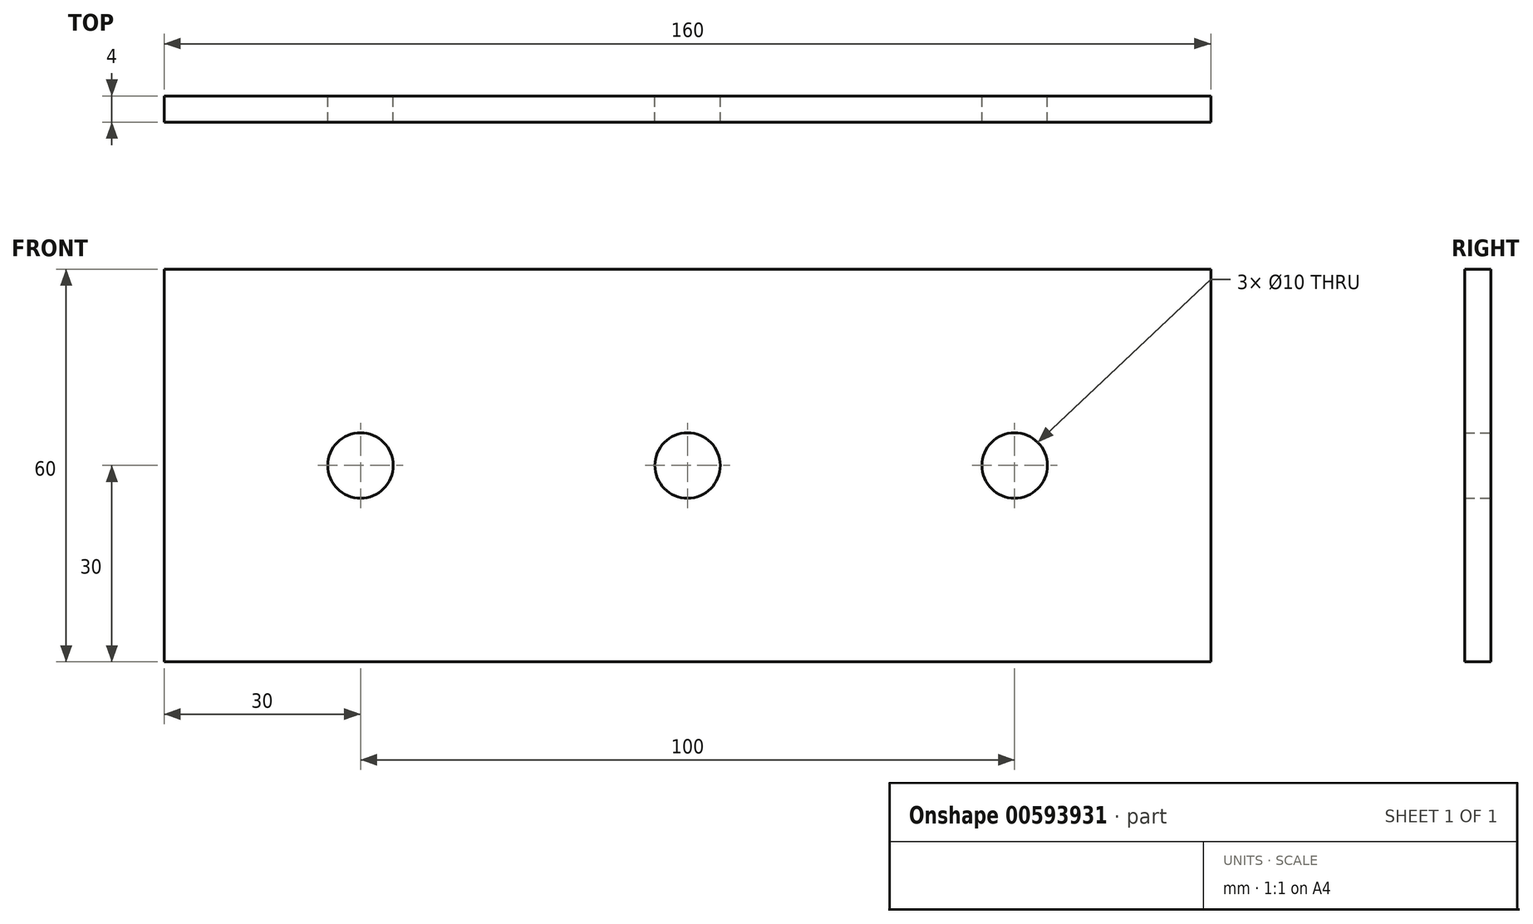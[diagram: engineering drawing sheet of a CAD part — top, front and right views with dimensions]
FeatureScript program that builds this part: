
annotation { "Feature Type Name" : "Feature", "Feature Type Description" : "" }
export const myFeature = defineFeature(function(context is Context, id is Id, definition is map)
    precondition{}
    {
        {
            var Q0;
            Q0=qCreatedBy(makeId("Front.planeOp"),FACE);
            var sketch = newSketch(context, id + "F0", { "sketchPlane" : qUnion([Q0])});
            skLineSegment(sketch, "E0.bottom", {"start": v(-80, 30) * mm, "end": v(80, 30) * mm});
            skLineSegment(sketch, "E0.top", {"start": v(-80, -30) * mm, "end": v(80, -30) * mm});
            skLineSegment(sketch, "E0.left", {"start": v(-80, 30) * mm, "end": v(-80, -30) * mm});
            skLineSegment(sketch, "E0.right", {"start": v(80, 30) * mm, "end": v(80, -30) * mm});
            skCircle(sketch, "E1", {"center": v(0, 0) * mm, "radius": 5 * mm});
            skCircle(sketch, "E2", {"center": v(-50, 0) * mm, "radius": 5 * mm});
            skCircle(sketch, "E3.MirrorC", {"center": v(50, 0) * mm, "radius": 5 * mm});
            skSolve(sketch);
        }
        {
            var Q0;
            Q0=makeQuery(id+"F0.imprint","IMPRINT",FACE,{"disambiguationData":[TD([[makeQuery(id+"F0.imprint","IMPRINT",EDGE,{"derivedFrom":sQuery(id+"F0.wireOp",EDGE,"E0.bottom")}),-1.0]])]});
            extrude(context, id + "F1", {"entities" : qUnion([Q0]), "depth" : 4 * mm, "offsetDistance" : 25 * mm});
        }
    });
